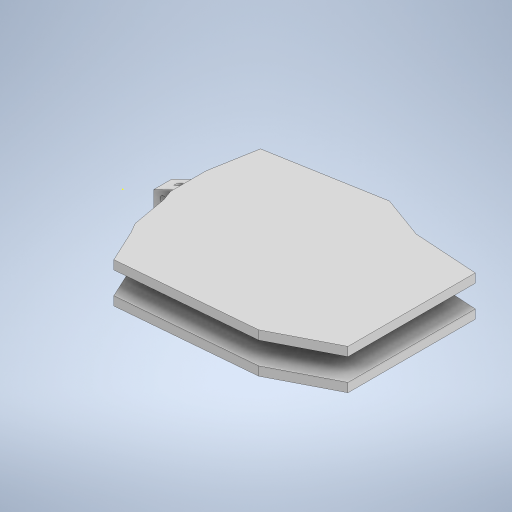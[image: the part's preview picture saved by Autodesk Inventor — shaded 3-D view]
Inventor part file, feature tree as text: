
AUTODESK INVENTOR PART (.ipt)
format: ipt  version: 2024 (Build 280153000, 153)  size: 454,144 bytes
history: native  units: mm
features: sketch x18, extrude x15, chamfer x3, move_body x3, other x2, plane x2, split x2, imported_body x2, delete_face x1
ambient origin geometry x8: Origin, YZ Plane, XZ Plane, XY Plane, X Axis, Y Axis, Z Axis, Center Point
bodies: Solid1 (feature_tree), Solid2 (feature_tree), Solid3 (feature_tree), Solid4 (feature_tree), Solid5 (feature_tree), Solid6 (feature_tree), Solid7 (feature_tree)
feature tree (48):
  other  "Repaired Geometry1"
  other  "Repaired Geometry2"
  extrude  "Extrusion1"  Depth=16.0mm
  sketch  "Sketch2"  dims[d2=15.0mm d3=0.0mm d4=10.0mm]
  extrude  "Extrusion2"  Depth=10.0mm
  chamfer  "Chamfer1"  Distance=21.25mm
  extrude  "Extrusion3"  Depth=10.0mm TaperAngle=0.0deg
  extrude  "Extrusion4"  Depth=11.5mm TaperAngle=0.0deg
  extrude  "Extrusion5"  Depth=1.0mm TaperAngle=0.0deg
  chamfer  "Chamfer2"  Distance=11.5mm Angle=45.0deg
  sketch  "Sketch6"  dims[d14=7.0mm d15=11.5mm d16=0.0mm]
  extrude  "Extrusion6"  Depth=9.0mm
  extrude  "Extrusion7"  Depth=11.5mm TaperAngle=0.0deg
  chamfer  "Chamfer3"  Distance=11.5mm Angle=45.0deg
  sketch  "Sketch9"  dims[d26=3.3mm d27=45.25mm d28=0.0mm d29=11.5mm d30=5.5mm d31=45.0deg]
  extrude  "Extrusion8"  Depth=65.75mm TaperAngle=0.0deg
  extrude  "Extrusion9"  Depth=9.0mm TaperAngle=0.0deg
  extrude  "Extrusion10"  Depth=13.0mm TaperAngle=0.0deg
  sketch  "Sketch13"  dims[d43=24.0mm d44=21.0mm d45=0.0mm]
  extrude  "Extrusion11"  Depth=21.0mm TaperAngle=0.0deg
  extrude  "Extrusion12"  TaperAngle=0.0deg  [1 undecoded]
  extrude  "Extrusion13"  Depth=8.0mm
  plane  "Work Plane1"
  split  "Split1"
  move_body  "Move Body1"
  extrude  "Extrusion14"  Depth=5.0mm
  delete_face  "Delete Face1"
  extrude  "Extrusion15"  Depth=16.0mm
  plane  "Work Plane2"
  split  "Split2"
  move_body  "Move Body2"
  move_body  "Move Body3"
  sketch  "Sketch1"  dims[d0=36.0mm d1=16.0mm]
  sketch  "Sketch3"  dims[d5=10.0mm]
  sketch  "Sketch4"  dims[d6=3.3mm d7=21.25mm d8=0.0mm]
  sketch  "Sketch5"  dims[d9=10.0mm d10=5.5mm d11=45.0deg d12=10.0mm d13=0.0mm]
  sketch  "Sketch7"  dims[d17=3.3mm d18=1.0mm d19=0.0mm d20=6.0mm d21=11.5mm d22=45.0deg]
  sketch  "Sketch8"  dims[d23=15.0mm d24=0.0mm d25=9.0mm]
  sketch  "Sketch10"  dims[d32=2.0mm d33=65.75mm d34=0.0mm]
  sketch  "Sketch11"  dims[d35=0.5mm d36=0.0mm d37=9.0mm d38=0.0mm]
  sketch  "Sketch12"  dims[d39=0.5mm d40=0.0mm d41=13.0mm d42=0.0mm]
  sketch  "Sketch14"  dims[d46=12.25mm d47=-12.0mm d48=0.0mm d49=0.0mm]
  sketch  "Sketch15"  dims[d50=10.0mm d51=0.0mm d52=8.0mm]
  sketch  "Sketch16"  dims[d53=16.0mm d54=5.0mm]
  sketch  "Sketch17"  dims[d55=19.198622mm d56=16.0mm]
  sketch  "Sketch18"  dims[d57=5.0mm d58=27.925268mm d59=16.0mm d60=20.071286mm d61=5.0mm d62=17.453293mm d63=16.0mm d64=180.0deg d65=50.0mm d66=29.670597mm d67=20.0mm d68=27.925268mm d70=60.0mm d71=30.543262mm d72=4.0mm d73=0.0mm d74=16.25mm d75=0.0mm d76=14.0mm d77=0.0mm d78=30.0mm d79=1.5mm d80=0.0mm]
  imported_body  "Base1"
  imported_body  "Base2"
note: 1 required parameter value undecoded (feature->parameter linkage not recoverable at this tier; creation-order binding heuristic only, values carry confidence <= 0.55)
